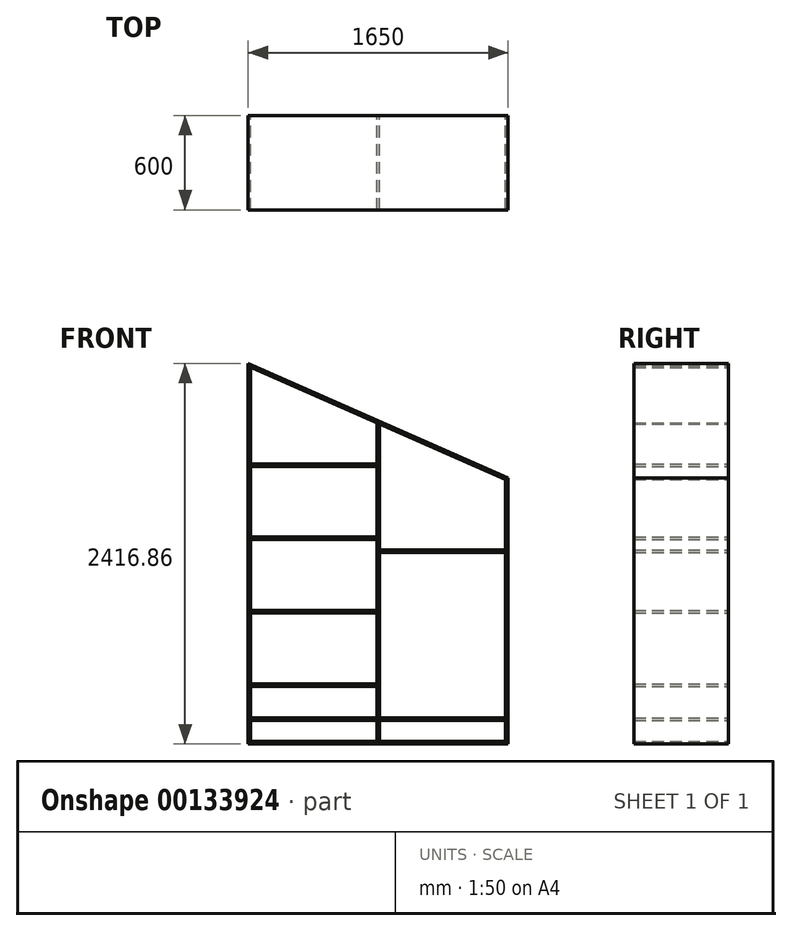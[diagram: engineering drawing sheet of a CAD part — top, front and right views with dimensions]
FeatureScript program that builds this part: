
annotation { "Feature Type Name" : "Feature", "Feature Type Description" : "" }
export const myFeature = defineFeature(function(context is Context, id is Id, definition is map)
    precondition{}
    {
        {
            var Q0;
            Q0=qCreatedBy(makeId("Front.planeOp"),FACE);
            var sketch = newSketch(context, id + "F0", { "sketchPlane" : qUnion([Q0])});
            skLineSegment(sketch, "E0", {"start": v(-19505.84, 25077.39) * mm, "end": v(-21155.84, 25077.39) * mm});
            skLineSegment(sketch, "E1", {"start": v(-21155.84, 25077.39) * mm, "end": v(-21155.84, 27494.25) * mm});
            skLineSegment(sketch, "E2", {"start": v(-21155.84, 27494.25) * mm, "end": v(-19505.84, 26767.39) * mm});
            skLineSegment(sketch, "E3", {"start": v(-19505.84, 25077.39) * mm, "end": v(-19505.84, 26767.39) * mm});
            skLineSegment(sketch, "E4", {"start": v(-19505.84, 26767.39) * mm, "end": v(-19505.84, 26847.39) * mm, "construction": true});
            skLineSegment(sketch, "E5", {"start": v(-19505.84, 26767.39) * mm, "end": v(-18535.84, 26767.39) * mm, "construction": true});
            skLineSegment(sketch, "E6", {"start": v(-20981.37, 27417.39) * mm, "end": v(-20981.37, 27497.39) * mm, "construction": true});
            skLineSegment(sketch, "E7.0", {"start": v(-19521.84, 25093.39) * mm, "end": v(-21139.84, 25093.39) * mm});
            skLineSegment(sketch, "E7.1", {"start": v(-19521.84, 25093.39) * mm, "end": v(-19521.84, 26756.95) * mm});
            skLineSegment(sketch, "E7.2", {"start": v(-21139.84, 27469.72) * mm, "end": v(-19521.84, 26756.95) * mm});
            skLineSegment(sketch, "E7.3", {"start": v(-21139.84, 25093.39) * mm, "end": v(-21139.84, 27469.72) * mm});
            skLineSegment(sketch, "E8", {"start": v(-20338.84, 25093.39) * mm, "end": v(-20338.84, 27116.86) * mm});
            skLineSegment(sketch, "E9", {"start": v(-20322.84, 27109.81) * mm, "end": v(-20322.84, 25093.39) * mm});
            skLineSegment(sketch, "E10", {"start": v(-21139.84, 25227.39) * mm, "end": v(-20338.84, 25227.39) * mm});
            skLineSegment(sketch, "E11", {"start": v(-21139.84, 25243.39) * mm, "end": v(-20338.84, 25243.39) * mm});
            skLineSegment(sketch, "E12.0.1.0", {"start": v(-21139.84, 25459.39) * mm, "end": v(-20338.84, 25459.39) * mm});
            skLineSegment(sketch, "E12.0.1.1", {"start": v(-21139.84, 25443.39) * mm, "end": v(-20338.84, 25443.39) * mm});
            skLineSegment(sketch, "E12.0.2.0", {"start": v(-21139.84, 25925.39) * mm, "end": v(-20338.84, 25925.39) * mm});
            skLineSegment(sketch, "E12.0.2.1", {"start": v(-21139.84, 25909.39) * mm, "end": v(-20338.84, 25909.39) * mm});
            skLineSegment(sketch, "E12.direction2", {"start": v(-21139.84, 25227.39) * mm, "end": v(-21139.84, 25443.39) * mm, "construction": true});
            skLineSegment(sketch, "E13.0.0.3", {"start": v(-21139.84, 26391.39) * mm, "end": v(-20338.84, 26391.39) * mm});
            skLineSegment(sketch, "E13.3.0.3", {"start": v(-21139.84, 26375.39) * mm, "end": v(-20338.84, 26375.39) * mm});
            skLineSegment(sketch, "E13.0.0.4", {"start": v(-21139.84, 26857.39) * mm, "end": v(-20338.84, 26857.39) * mm});
            skLineSegment(sketch, "E13.3.0.4", {"start": v(-21139.84, 26841.39) * mm, "end": v(-20338.84, 26841.39) * mm});
            skLineSegment(sketch, "E14", {"start": v(-20671.15, 27614.74) * mm, "end": v(-20243.07, 27614.74) * mm});
            skLineSegment(sketch, "E15", {"start": v(-20322.84, 25227.39) * mm, "end": v(-19521.84, 25227.39) * mm});
            skLineSegment(sketch, "E16", {"start": v(-19521.84, 25243.39) * mm, "end": v(-20322.84, 25243.39) * mm});
            skLineSegment(sketch, "E17", {"start": v(-20322.84, 26293.39) * mm, "end": v(-19521.84, 26293.39) * mm});
            skLineSegment(sketch, "E18", {"start": v(-19521.84, 26309.39) * mm, "end": v(-20322.84, 26309.39) * mm});
            skPoint(sketch, "E19", {"position": v(-19505.84, 25077.39) * mm});
            skLineSegment(sketch, "E20", {"start": v(-21139.84, 25077.39) * mm, "end": v(-21139.84, 25093.39) * mm});
            skLineSegment(sketch, "E21", {"start": v(-21139.84, 27469.72) * mm, "end": v(-21155.84, 27476.76) * mm});
            skLineSegment(sketch, "E22", {"start": v(-19521.84, 26756.95) * mm, "end": v(-19505.84, 26767.39) * mm});
            skLineSegment(sketch, "E23", {"start": v(-19521.84, 25093.39) * mm, "end": v(-19521.84, 25077.39) * mm});
            skSolve(sketch);
        }
        {
            var Q0;
            {var subQ11=sQuery(id+"F0.wireOp",EDGE,"E20");Q0=makeQuery(id+"F0.imprint","IMPRINT",FACE,{"disambiguationData":[TD([[makeQuery(id+"F0.imprint","IMPRINT",EDGE,{"derivedFrom":subQ11}),1.0]])]});}
            extrude(context, id + "F1", {"entities" : qUnion([Q0]), "depth" : 600 * mm});
        }
        {
            var Q0;
            {var subQ3=sQuery(id+"F0.wireOp",EDGE,"E2");Q0=makeQuery(id+"F0.imprint","IMPRINT",FACE,{"disambiguationData":[TD([[makeQuery(id+"F0.imprint","IMPRINT",EDGE,{"derivedFrom":subQ3}),-1.0]])]});}
            extrude(context, id + "F2", {"entities" : qUnion([Q0]), "depth" : 600 * mm});
        }
        {
            var Q0;
            {var subQ4=sQuery(id+"F0.wireOp",EDGE,"E3");Q0=makeQuery(id+"F0.imprint","IMPRINT",FACE,{"disambiguationData":[TD([[makeQuery(id+"F0.imprint","IMPRINT",EDGE,{"derivedFrom":subQ4}),1.0]])]});}
            extrude(context, id + "F3", {"entities" : qUnion([Q0]), "depth" : 600 * mm});
        }
        {
            var Q0;
            {var subQ0=sQuery(id+"F0.wireOp",EDGE,"E20");Q0=makeQuery(id+"F0.imprint","IMPRINT",FACE,{"disambiguationData":[TD([[makeQuery(id+"F0.imprint","IMPRINT",EDGE,{"derivedFrom":subQ0}),-1.0]])]});}
            extrude(context, id + "F4", {"entities" : qUnion([Q0]), "depth" : 600 * mm});
        }
        {
            var Q0;
            {var subQ0=sQuery(id+"F0.wireOp",EDGE,"E8");var subQ10=sQuery(id+"F0.wireOp",EDGE,"E7.0");var subQ11=makeQuery(id+"F0.imprint","INTERSECT",VERTEX,{"derivedFrom":[subQ10,subQ0]});Q0=makeQuery(id+"F0.imprint","IMPRINT",FACE,{"disambiguationData":[TD([[makeQuery(id+"F0.imprint","IMPRINT",EDGE,{"disambiguationData":[TD([[subQ11,1.0]])],"derivedFrom":subQ10}),-1.0]])]});}
            extrude(context, id + "F5", {"entities" : qUnion([Q0]), "depth" : 600 * mm});
        }
        {
            var Q0;
            {var subQ0=sQuery(id+"F0.wireOp",EDGE,"E10");Q0=makeQuery(id+"F0.imprint","IMPRINT",FACE,{"disambiguationData":[TD([[makeQuery(id+"F0.imprint","IMPRINT",EDGE,{"derivedFrom":subQ0}),1.0]])]});}
            var Q1;
            {var subQ0=sQuery(id+"F0.wireOp",EDGE,"E15");Q1=makeQuery(id+"F0.imprint","IMPRINT",FACE,{"disambiguationData":[TD([[makeQuery(id+"F0.imprint","IMPRINT",EDGE,{"derivedFrom":subQ0}),1.0]])]});}
            var Q2;
            {var subQ0=sQuery(id+"F0.wireOp",EDGE,"E12.0.1.0");Q2=makeQuery(id+"F0.imprint","IMPRINT",FACE,{"disambiguationData":[TD([[makeQuery(id+"F0.imprint","IMPRINT",EDGE,{"derivedFrom":subQ0}),-1.0]])]});}
            var Q3;
            {var subQ0=sQuery(id+"F0.wireOp",EDGE,"E12.0.2.0");Q3=makeQuery(id+"F0.imprint","IMPRINT",FACE,{"disambiguationData":[TD([[makeQuery(id+"F0.imprint","IMPRINT",EDGE,{"derivedFrom":subQ0}),-1.0]])]});}
            var Q4;
            {var subQ0=sQuery(id+"F0.wireOp",EDGE,"E17");Q4=makeQuery(id+"F0.imprint","IMPRINT",FACE,{"disambiguationData":[TD([[makeQuery(id+"F0.imprint","IMPRINT",EDGE,{"derivedFrom":subQ0}),1.0]])]});}
            var Q5;
            {var subQ0=sQuery(id+"F0.wireOp",EDGE,"E13.0.0.3");Q5=makeQuery(id+"F0.imprint","IMPRINT",FACE,{"disambiguationData":[TD([[makeQuery(id+"F0.imprint","IMPRINT",EDGE,{"derivedFrom":subQ0}),-1.0]])]});}
            var Q6;
            {var subQ0=sQuery(id+"F0.wireOp",EDGE,"E13.0.0.4");Q6=makeQuery(id+"F0.imprint","IMPRINT",FACE,{"disambiguationData":[TD([[makeQuery(id+"F0.imprint","IMPRINT",EDGE,{"derivedFrom":subQ0}),-1.0]])]});}
            extrude(context, id + "F6", {"entities" : qUnion([Q0, Q1, Q2, Q3, Q4, Q5, Q6]), "depth" : 600 * mm});
        }
    });
